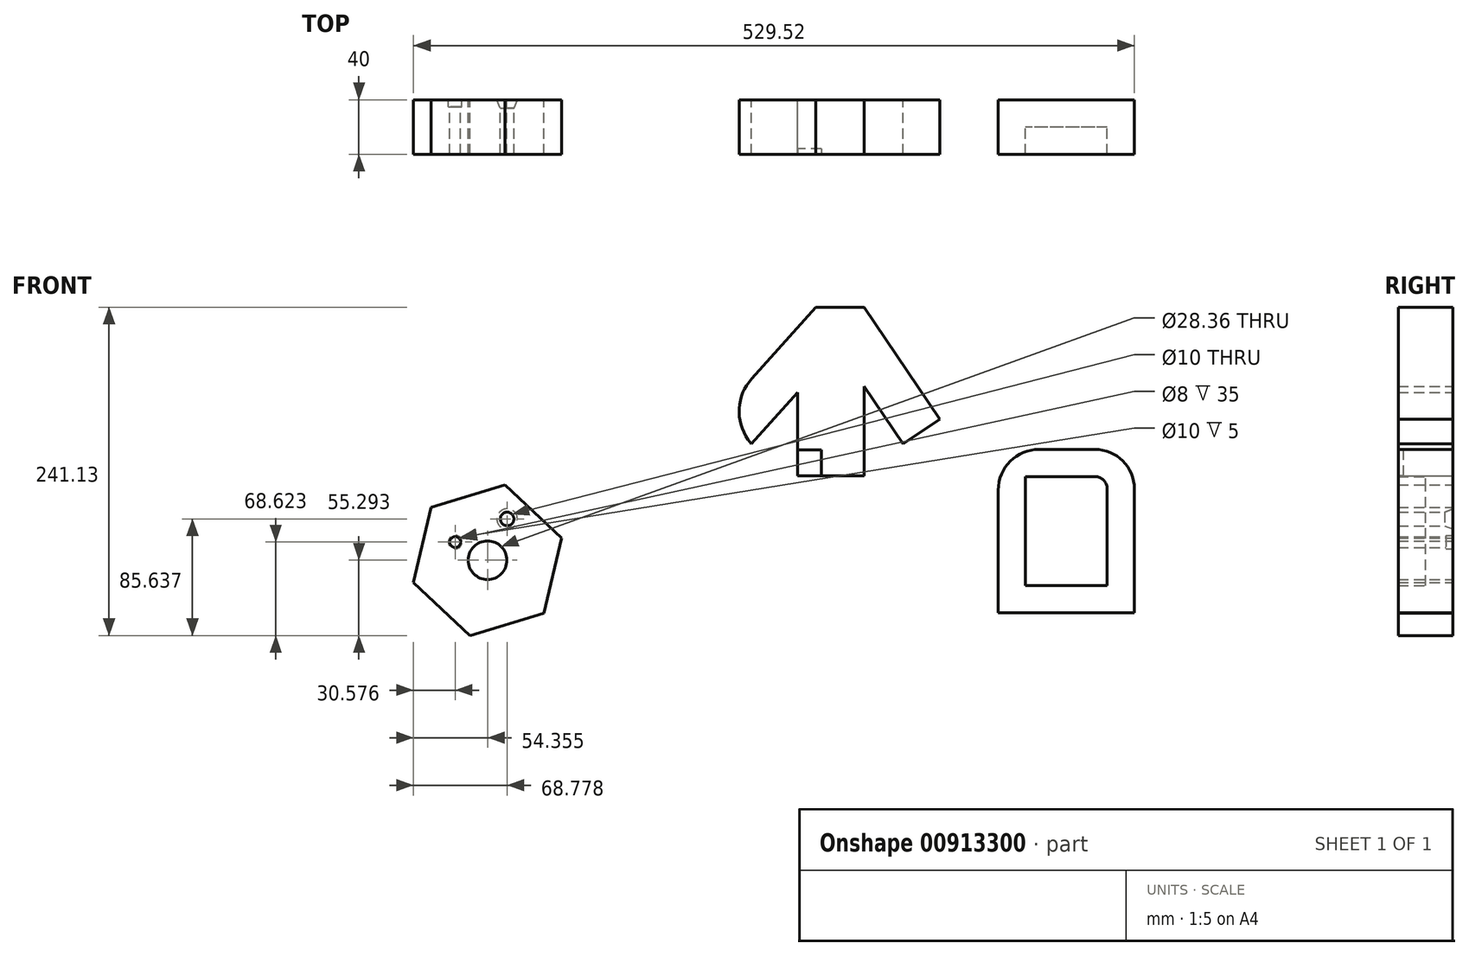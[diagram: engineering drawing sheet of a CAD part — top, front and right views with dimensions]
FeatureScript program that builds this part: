
annotation { "Feature Type Name" : "Feature", "Feature Type Description" : "" }
export const myFeature = defineFeature(function(context is Context, id is Id, definition is map)
    precondition{}
    {
        {
            var Q0;
            Q0=qCreatedBy(makeId("Front.planeOp"),FACE);
            var sketch = newSketch(context, id + "F0", { "sketchPlane" : qUnion([Q0])});
            skLineSegment(sketch, "E0.bottom", {"start": v(50, -60) * mm, "end": v(-50, -60) * mm});
            skLineSegment(sketch, "E0.top", {"start": v(50, 60) * mm, "end": v(-50, 60) * mm});
            skLineSegment(sketch, "E0.left", {"start": v(50, -60) * mm, "end": v(50, 60) * mm});
            skLineSegment(sketch, "E0.right", {"start": v(-50, -60) * mm, "end": v(-50, 60) * mm});
            skPoint(sketch, "E0.middle", {"position": v(0, 0) * mm});
            skLineSegment(sketch, "E1", {"start": v(-250.18, 90.72) * mm, "end": v(-183.9, 164.35) * mm});
            skLineSegment(sketch, "E2", {"start": v(-183.9, 164.35) * mm, "end": v(-148.59, 164.35) * mm});
            skLineSegment(sketch, "E3", {"start": v(-148.59, 164.35) * mm, "end": v(-93.06, 82.3) * mm});
            skLineSegment(sketch, "E4", {"start": v(-93.06, 82.3) * mm, "end": v(-120.03, 64.05) * mm});
            skLineSegment(sketch, "E5", {"start": v(-120.03, 64.05) * mm, "end": v(-148.59, 106.25) * mm});
            skLineSegment(sketch, "E6", {"start": v(-148.59, 106.25) * mm, "end": v(-148.59, 40.7) * mm});
            skLineSegment(sketch, "E7", {"start": v(-148.59, 40.7) * mm, "end": v(-197.4, 40.7) * mm});
            skLineSegment(sketch, "E8", {"start": v(-197.4, 40.7) * mm, "end": v(-197.4, 101.92) * mm});
            skLineSegment(sketch, "E9", {"start": v(-197.4, 101.92) * mm, "end": v(-231.5, 64.05) * mm});
            skLineSegment(sketch, "E10", {"start": v(-231.5, 64.05) * mm, "end": v(-250.18, 90.72) * mm});
            skCircle(sketch, "E11.cCircle", {"center": v(-425.16, -21.49) * mm, "radius": 49.18 * mm, "construction": true});
            skLineSegment(sketch, "E11.0", {"start": v(-383.75, -60.34) * mm, "end": v(-438.1, -76.78) * mm});
            skLineSegment(sketch, "E11.1", {"start": v(-438.1, -76.78) * mm, "end": v(-479.52, -37.93) * mm});
            skLineSegment(sketch, "E11.2", {"start": v(-479.52, -37.93) * mm, "end": v(-466.58, 17.36) * mm});
            skLineSegment(sketch, "E11.3", {"start": v(-466.58, 17.36) * mm, "end": v(-412.23, 33.8) * mm});
            skLineSegment(sketch, "E11.4", {"start": v(-412.23, 33.8) * mm, "end": v(-370.8, -5.04) * mm});
            skLineSegment(sketch, "E11.5", {"start": v(-370.8, -5.04) * mm, "end": v(-383.75, -60.34) * mm});
            skPoint(sketch, "E11.0.midPoint", {"position": v(-410.92, -68.56) * mm});
            skCircle(sketch, "E12.0", {"center": v(-425.16, -21.49) * mm, "radius": 14.18 * mm});
            skPoint(sketch, "E13", {"position": v(-410.74, 8.86) * mm});
            skPoint(sketch, "E14", {"position": v(-448.94, -8.16) * mm});
            skSolve(sketch);
        }
        {
            var Q0;
            Q0 = qSketchRegion(id + "F0", true);
            extrude(context, id + "F1", {"entities" : qUnion([Q0]), "depth" : 40 * mm, "offsetDistance" : 25.4 * mm});
        }
        {
            var Q0;
            Q0=makeQuery(id+"F1.opExtrude","SWEPT_EDGE",EDGE,{"disambiguationData":[OSD([sQuery(id+"F0.wireOp",EDGE,"E0.top"),sQuery(id+"F0.wireOp",EDGE,"E0.left")])]});
            fillet(context, id + "F2", {"entities" : qUnion([Q0]), "radius" : 28.97 * mm, "tangentPropagation" : true, "allowEdgeOverflow" : false});
        }
        {
            var Q0;
            Q0=makeQuery(id+"F1.opExtrude","CAP_FACE",FACE,{"disambiguationData":[OSD([sQuery(id+"F0.wireOp",EDGE,"E0.bottom"),sQuery(id+"F0.wireOp",EDGE,"E0.top"),sQuery(id+"F0.wireOp",EDGE,"E0.left"),sQuery(id+"F0.wireOp",EDGE,"E0.right")])],"isStart":false});
            shell(context, id + "F3", {"entities" : qUnion([Q0]), "thickness" : 20 * mm});
        }
        {
            var Q0;
            Q0=makeQuery(id+"F1.opExtrude","SWEPT_EDGE",EDGE,{"disambiguationData":[OSD([sQuery(id+"F0.wireOp",EDGE,"E0.top"),sQuery(id+"F0.wireOp",EDGE,"E0.right")])]});
            fillet(context, id + "F4", {"entities" : qUnion([Q0]), "radius" : 30 * mm, "tangentPropagation" : true, "allowEdgeOverflow" : false});
        }
        {
            var Q0;
            Q0=makeQuery(id+"F1.opExtrude","CAP_FACE",FACE,{"disambiguationData":[OSD([sQuery(id+"F0.wireOp",EDGE,"E11.0"),sQuery(id+"F0.wireOp",EDGE,"E11.1"),sQuery(id+"F0.wireOp",EDGE,"E11.2"),sQuery(id+"F0.wireOp",EDGE,"E11.3"),sQuery(id+"F0.wireOp",EDGE,"E11.4"),sQuery(id+"F0.wireOp",EDGE,"E11.5"),sQuery(id+"F0.wireOp",EDGE,"E12.0")])],"isStart":false});
            var sketch = newSketch(context, id + "F5", { "sketchPlane" : qUnion([Q0])});
            skSolve(sketch);
        }
        {
            var Q0;
            Q0 = qSketchRegion(id + "F5", true);
            var Q1;
            Q1=makeQuery(id+"F5.imprint","IMPRINT",FACE,{"disambiguationData":[TD([[makeQuery(id+"F5.imprint","IMPRINT",EDGE,{"derivedFrom":makeQuery(id+"F1.opExtrude","CAP_EDGE",EDGE,{"disambiguationData":[OSD([sQuery(id+"F0.wireOp",EDGE,"E11.0")])],"isStart":false})}),-1.0]])]});
            var Q2;
            Q2=makeQuery(id+"F0.imprint","IMPRINT",FACE,{"disambiguationData":[TD([[makeQuery(id+"F0.imprint","IMPRINT",EDGE,{"derivedFrom":sQuery(id+"F0.wireOp",EDGE,"E11.0")}),-1.0]])]});
            extrude(context, id + "F6", {"entities" : qUnion([Q0, Q1, Q2]), "operationType" : NewBodyOperationType.ADD, "depth" : 9 * mm, "offsetDistance" : 25 * mm});
        }
        {
            var Q0;
            Q0=qCreatedBy(makeId("Front.planeOp"),FACE);
            cPlane(context, id + "F7", {"entities" : qUnion([Q0]), "cplaneType" : CPlaneType.OFFSET, "offset" : 71 * mm, "width" : 150 * mm, "height" : 150 * mm});
        }
        {
            var Q0;
            Q0=sQuery(id+"F0.wireOp",VERTEX,"E13");
            var Q1;
            Q1=makeQuery(id+"F1.opExtrude","SWEPT_BODY",BODY,{"disambiguationData":[OSD([sQuery(id+"F0.wireOp",EDGE,"E11.0"),sQuery(id+"F0.wireOp",EDGE,"E11.1"),sQuery(id+"F0.wireOp",EDGE,"E11.2"),sQuery(id+"F0.wireOp",EDGE,"E11.3"),sQuery(id+"F0.wireOp",EDGE,"E11.4"),sQuery(id+"F0.wireOp",EDGE,"E11.5"),sQuery(id+"F0.wireOp",EDGE,"E12.0")])]});
            hole(context, id + "F8", {"style" : HoleStyle.C_SINK, "endStyle" : HoleEndStyle.THROUGH, "oppositeDirection" : true, "holeDiameter" : 10 * mm, "cSinkDiameter" : 15 * mm, "cSinkAngle" : 45 * degree, "majorDiameter" : 5 * mm, "isTappedThrough" : true, "tappedDepth" : 12 * mm, "tapClearance" : 3, "locations" : qUnion([Q0]), "scope" : qUnion([Q1])});
        }
        {
            var Q0;
            Q0=makeQuery(id+"F1.opExtrude","SWEPT_EDGE",EDGE,{"disambiguationData":[OSD([sQuery(id+"F0.wireOp",EDGE,"E1"),sQuery(id+"F0.wireOp",EDGE,"E10")])]});
            fillet(context, id + "F9", {"entities" : qUnion([Q0]), "radius" : 36 * mm, "tangentPropagation" : true, "allowEdgeOverflow" : false});
        }
        {
            var Q0;
            Q0=sQuery(id+"F0.wireOp",VERTEX,"E14");
            var Q1;
            Q1=makeQuery(id+"F1.opExtrude","SWEPT_BODY",BODY,{"disambiguationData":[OSD([sQuery(id+"F0.wireOp",EDGE,"E11.0"),sQuery(id+"F0.wireOp",EDGE,"E11.1"),sQuery(id+"F0.wireOp",EDGE,"E11.2"),sQuery(id+"F0.wireOp",EDGE,"E11.3"),sQuery(id+"F0.wireOp",EDGE,"E11.4"),sQuery(id+"F0.wireOp",EDGE,"E11.5"),sQuery(id+"F0.wireOp",EDGE,"E12.0")])]});
            hole(context, id + "F10", {"style" : HoleStyle.C_BORE, "endStyle" : HoleEndStyle.THROUGH, "oppositeDirection" : true, "holeDiameter" : 8 * mm, "cBoreDiameter" : 10 * mm, "cBoreDepth" : 5 * mm, "majorDiameter" : 5 * mm, "isTappedThrough" : true, "tappedDepth" : 12 * mm, "tapClearance" : 3, "locations" : qUnion([Q0]), "scope" : qUnion([Q1])});
        }
        {
            var Q0;
            Q0=qCreatedBy(id+"F7.planeOp",FACE);
            var sketch = newSketch(context, id + "F11", { "sketchPlane" : qUnion([Q0])});
            skLineSegment(sketch, "E15.bottom", {"start": v(-219.2, 27.7) * mm, "end": v(-180.03, 27.7) * mm});
            skLineSegment(sketch, "E15.top", {"start": v(-219.2, 59.55) * mm, "end": v(-180.03, 59.55) * mm});
            skLineSegment(sketch, "E15.left", {"start": v(-219.2, 27.7) * mm, "end": v(-219.2, 59.55) * mm});
            skLineSegment(sketch, "E15.right", {"start": v(-180.03, 27.7) * mm, "end": v(-180.03, 59.55) * mm});
            skSolve(sketch);
        }
        {
            var Q0;
            Q0=makeQuery(id+"F11.imprint","IMPRINT",FACE,{"disambiguationData":[TD([[makeQuery(id+"F11.imprint","IMPRINT",EDGE,{"derivedFrom":sQuery(id+"F11.wireOp",EDGE,"E15.bottom")}),1.0]])]});
            extrude(context, id + "F12", {"entities" : qUnion([Q0]), "operationType" : NewBodyOperationType.REMOVE, "oppositeDirection" : true, "depth" : 35 * mm, "offsetDistance" : 25 * mm});
        }
    });
